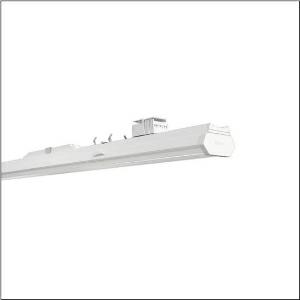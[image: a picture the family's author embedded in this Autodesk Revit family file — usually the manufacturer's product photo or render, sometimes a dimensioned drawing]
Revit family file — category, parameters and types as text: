
# Revit family: licross_r__11_protected_ho_51tp12dn4exld_5c83
name_source: partatom
category: Lighting Fixtures
units: mm (PartAtom-declared; Revit-internal decimal feet)

## family parameters
Cut with Voids When Loaded = No
Host = Face
Light Source = No
Part Type = Normal
Room Calculation Point = No
Round Connector Dimension = Use Diameter
Shared = No

## types (1)
- --- (1 x LED, 2220 lm, 14.7 W, 4000K)
    Apparent Load = 15 VA
    CIE Flux Codes = 70 91 97 98 100
    Color Rendering = 80
    Color Temperature = 4000K
    Default Elevation = 1800 mm
    Description = Licross® 11 Protected HOluminaire insert, length: 1.500mm, width: 90mm, height: 101mm, LED rated luminous flux: 14.070lm, light colour: 840, control gear: DALI 2, control gear: ECG DALI, with plug, 6-pole, with phase selection, mains connection: 220..240V, AC/DC, 0/50..60Hz, for central battery installations according to DIN EN 60598-2-22, for emergency light function, without changeover relay, halogen-free wiring, primary optical cover: cover, of PMMA, light emission: direct with ceiling illumination distribution, protection rating (complete): IP64, insulation class (complete): insulation class I (protective earthing), certification: CE, ENEC, VDE, protection symbol: D if used in an environment without relevant dust loads with corresponding accessories, permissible ambient temperature for indoor applications: -25..+35°C, standard: EN 60598-2-22, reducing of maximum allowable ambient temperature of 5°C with ceiling mounting, corresponds to IFS (International Featured Standards) requirements for safety and quality in the food industry, packaging unit: 1 piece
    Height = 92 mm
    Lamp = 1 x LED
    Lamp Light Flux = 2220 lm
    Lamp Power = 14.7 W
    Lamp count = 1
    Length = 1500 mm
    Luminous efficacy = 151 lm/W
    Manufacturer = Siteco
    ModVariant = No
    Model = 51TP12DN4EXLD
    Mounting Place = Ceiling
    Mounting Type = Pendant
    Number of Poles = 1
    OnlyDefault = Yes
    Power Factor = 1
    Product Name = Licross® 11 Protected HO
    Product group = luminaire insert
    ProductGroupID = 902
    Protection Class = Protection class I
    Protection Degree = IP 64
    RLX_Detail_Level = 1
    RlxData = <blob elided: 24461 chars, md5=3186a100>
    Socket = socket
    Standby Power = 0 W
    System Light Flux = 2220 lm
    System Power = 15 W
    Type Comments = : DC mode (central or group accumulator) initial emergency light level
    Type Image = l_1256148.jpg
    URL = http://relux.com
    VarID = @adj_134769
    Voltage = 0 V
    Weight = 0.00 kg
    Width = 88 mm

## geometry (parser evidence)
native form markers: Blend x4, Sweep x13
no freeform markers — native parametric forms only
